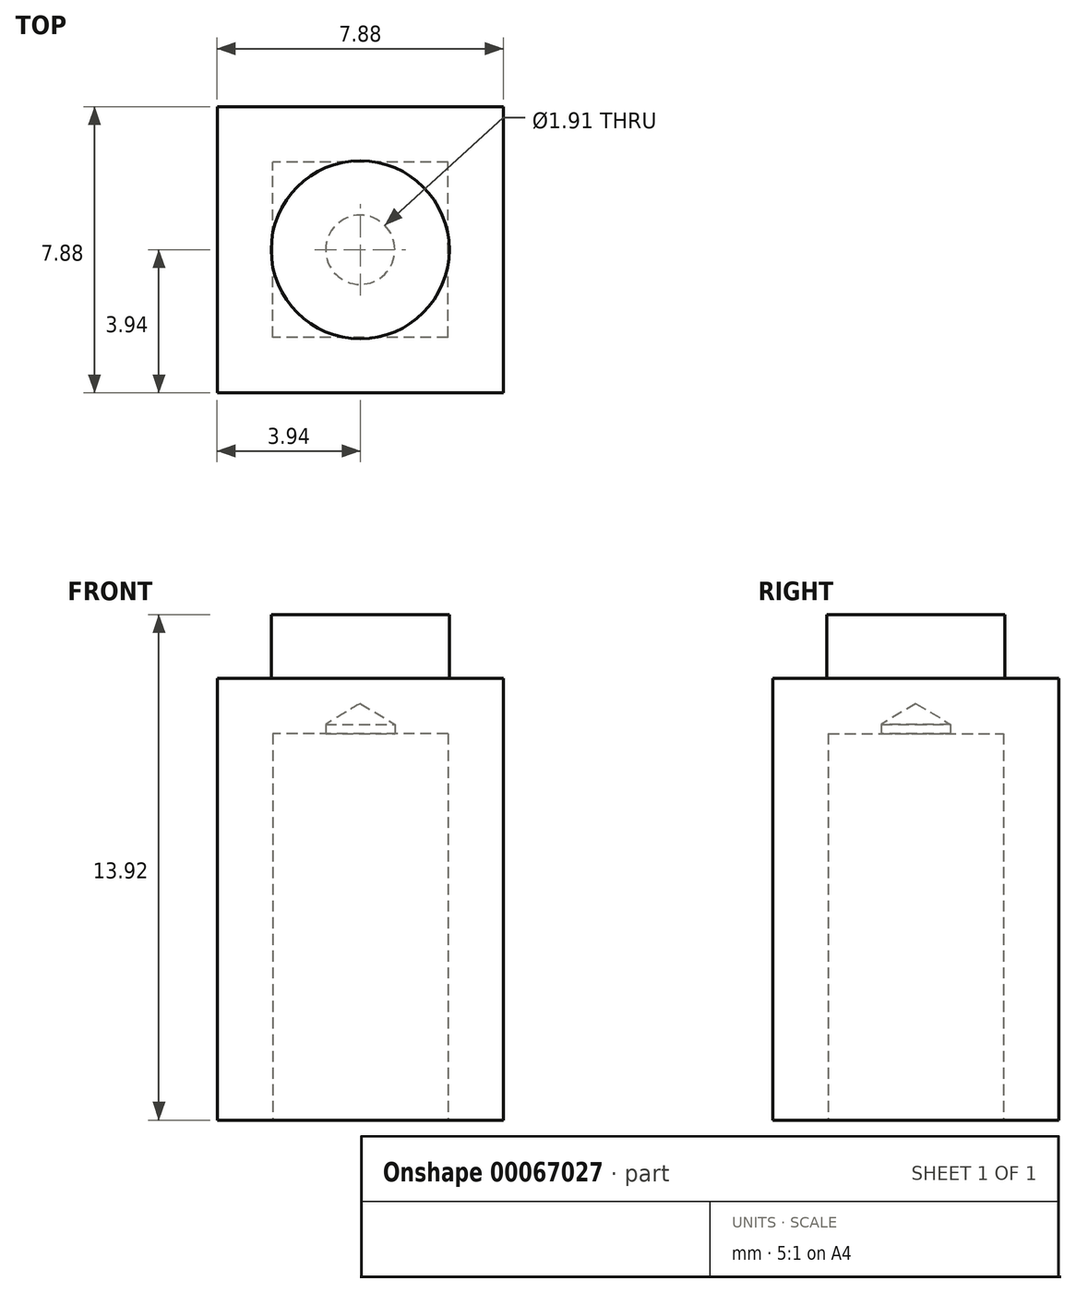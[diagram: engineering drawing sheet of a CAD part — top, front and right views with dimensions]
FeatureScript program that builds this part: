
annotation { "Feature Type Name" : "Feature", "Feature Type Description" : "" }
export const myFeature = defineFeature(function(context is Context, id is Id, definition is map)
    precondition{}
    {
        {
            var Q0;
            Q0=qCreatedBy(makeId("Top.planeOp"),FACE);
            var sketch = newSketch(context, id + "F0", { "sketchPlane" : qUnion([Q0])});
            skLineSegment(sketch, "E0.rect.bottom", {"start": v(3.94, -3.94) * mm, "end": v(-3.94, -3.94) * mm});
            skLineSegment(sketch, "E0.rect.top", {"start": v(3.94, 3.94) * mm, "end": v(-3.94, 3.94) * mm});
            skLineSegment(sketch, "E0.rect.left", {"start": v(3.94, -3.94) * mm, "end": v(3.94, 3.94) * mm});
            skLineSegment(sketch, "E0.rect.right", {"start": v(-3.94, -3.94) * mm, "end": v(-3.94, 3.94) * mm});
            skPoint(sketch, "E0.rect.middle", {"position": v(0, 0) * mm});
            skSolve(sketch);
        }
        {
            var Q0;
            Q0 = qSketchRegion(id + "F0", true);
            extrude(context, id + "F1", {"entities" : qUnion([Q0]), "depth" : 12.17 * mm});
        }
        {
            var Q0;
            Q0=makeQuery(id+"F1.opExtrude","CAP_FACE",FACE,{"disambiguationData":[OSD([sQuery(id+"F0.wireOp",EDGE,"E0.rect.bottom"),sQuery(id+"F0.wireOp",EDGE,"E0.rect.top"),sQuery(id+"F0.wireOp",EDGE,"E0.rect.left"),sQuery(id+"F0.wireOp",EDGE,"E0.rect.right")])],"isStart":true});
            shell(context, id + "F2", {"entities" : qUnion([Q0]), "thickness" : 1.52 * mm});
        }
        {
            var Q0;
            Q0=makeQuery(id+"F2.opShell","OFFSET_FACE",FACE,{"disambiguationData":[OSD([sQuery(id+"F0.wireOp",EDGE,"E0.rect.bottom"),sQuery(id+"F0.wireOp",EDGE,"E0.rect.top"),sQuery(id+"F0.wireOp",EDGE,"E0.rect.left"),sQuery(id+"F0.wireOp",EDGE,"E0.rect.right")])]});
            var sketch = newSketch(context, id + "F3", { "sketchPlane" : qUnion([Q0])});
            skCircle(sketch, "E1", {"center": v(0, 0) * mm, "radius": 0.95 * mm});
            skSolve(sketch);
        }
        {
            var Q0;
            Q0=sQuery(id+"F3.wireOp",VERTEX,"E1.center");
            var Q1;
            Q1=makeQuery(id+"F1.opExtrude","SWEPT_BODY",BODY,{"disambiguationData":[OSD([sQuery(id+"F0.wireOp",EDGE,"E0.rect.bottom"),sQuery(id+"F0.wireOp",EDGE,"E0.rect.top"),sQuery(id+"F0.wireOp",EDGE,"E0.rect.left"),sQuery(id+"F0.wireOp",EDGE,"E0.rect.right")])]});
            hole(context, id + "F4", {"style" : HoleStyle.SIMPLE, "holeDiameter" : 1.9 * mm, "endStyle" : HoleEndStyle.BLIND, "holeDepth" : 0.25 * mm, "locations" : qUnion([Q0]), "scope" : qUnion([Q1])});
        }
        {
            var Q0;
            Q0=makeQuery(id+"F1.opExtrude","CAP_FACE",FACE,{"disambiguationData":[OSD([sQuery(id+"F0.wireOp",EDGE,"E0.rect.bottom"),sQuery(id+"F0.wireOp",EDGE,"E0.rect.top"),sQuery(id+"F0.wireOp",EDGE,"E0.rect.left"),sQuery(id+"F0.wireOp",EDGE,"E0.rect.right")])],"isStart":false});
            var sketch = newSketch(context, id + "F5", { "sketchPlane" : qUnion([Q0])});
            skCircle(sketch, "E2", {"center": v(0, 0) * mm, "radius": 2.45 * mm});
            skSolve(sketch);
        }
        {
            var Q0;
            Q0 = qSketchRegion(id + "F5", true);
            extrude(context, id + "F6", {"entities" : qUnion([Q0]), "operationType" : NewBodyOperationType.ADD, "depth" : 1.75 * mm});
        }
    });
